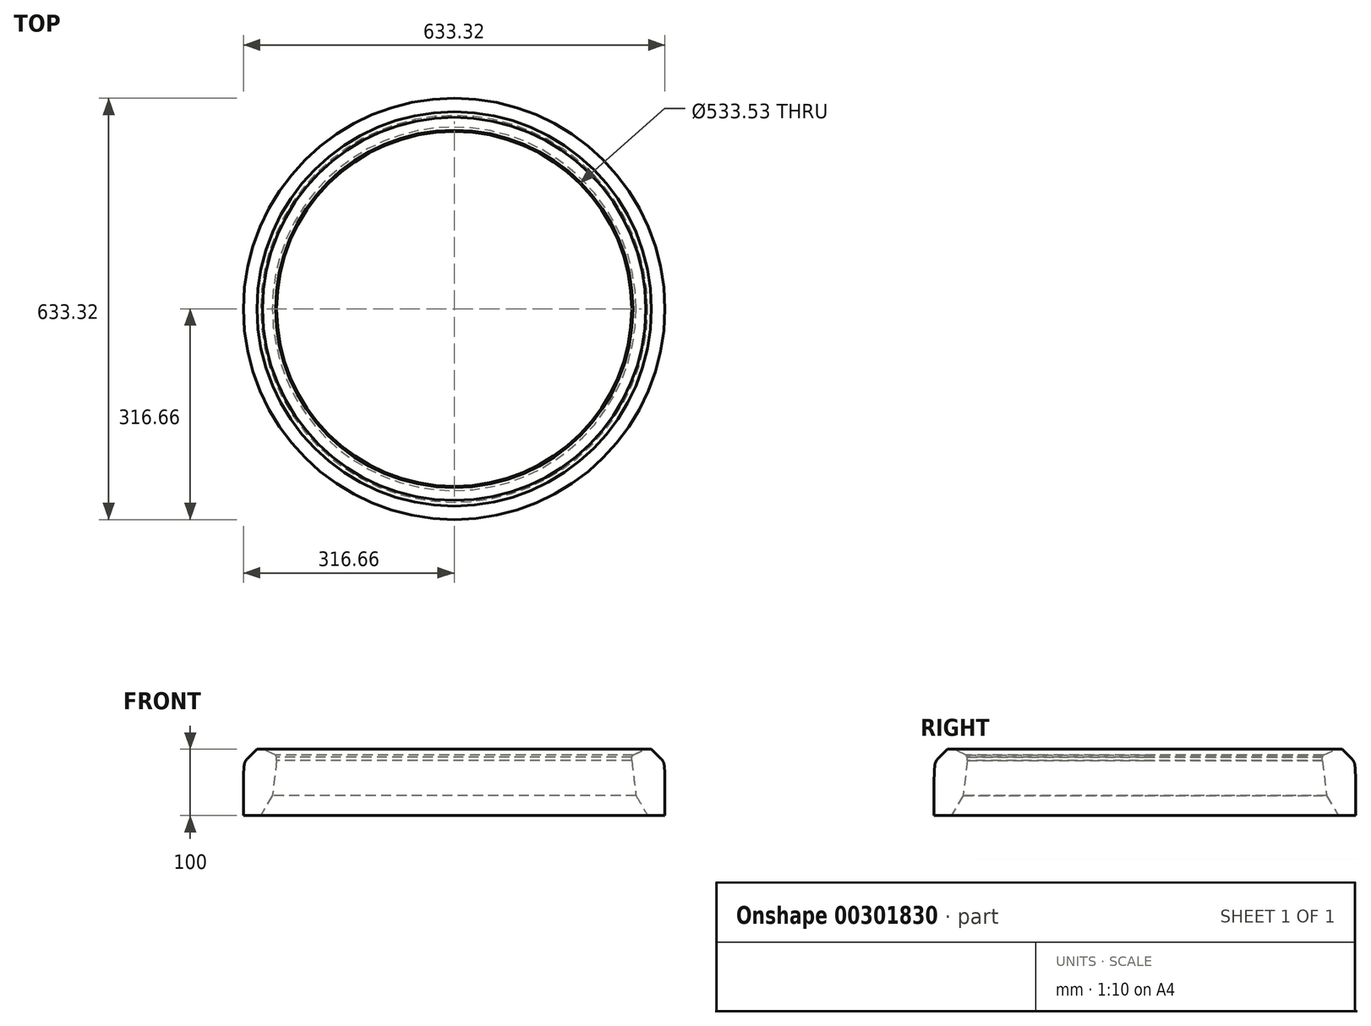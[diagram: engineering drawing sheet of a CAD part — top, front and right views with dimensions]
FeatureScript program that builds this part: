
annotation { "Feature Type Name" : "Feature", "Feature Type Description" : "" }
export const myFeature = defineFeature(function(context is Context, id is Id, definition is map)
    precondition{}
    {
        {
            var Q0;
            Q0=qCreatedBy(makeId("Front.planeOp"),FACE);
            var sketch = newSketch(context, id + "F0", { "sketchPlane" : qUnion([Q0])});
            skLineSegment(sketch, "E0", {"start": v(0, 0) * mm, "end": v(0, 100) * mm});
            skLineSegment(sketch, "E1", {"start": v(-316.65, 55) * mm, "end": v(-316.65, 0) * mm});
            skLineSegment(sketch, "E2", {"start": v(-290.69, 0) * mm, "end": v(-316.66, 0) * mm});
            skLineSegment(sketch, "E3", {"start": v(-296.34, 100) * mm, "end": v(-288, 100) * mm});
            skArc(sketch, "E4", {"start": v(-315.58, 75.7) * mm, "mid": v(-316.39, 65.36) * mm, "end": v(-316.65, 55) * mm});
            skArc(sketch, "E5", {"start": v(-310.98, 85.35) * mm, "mid": v(-314.11, 80.92) * mm, "end": v(-315.58, 75.7) * mm});
            skLineSegment(sketch, "E6", {"start": v(-296.34, 100) * mm, "end": v(-310.98, 85.35) * mm});
            skLineSegment(sketch, "E7", {"start": v(-288, 100) * mm, "end": v(-268.6, 90.95) * mm});
            skLineSegment(sketch, "E8", {"start": v(-266.76, 83) * mm, "end": v(-273.25, 30.2) * mm});
            skPoint(sketch, "E9.endSnap0", {"position": v(-268.21, 90.77) * mm});
            skLineSegment(sketch, "E10.trimOffspring", {"start": v(-268.6, 90.95) * mm, "end": v(-266.77, 87.77) * mm});
            skLineSegment(sketch, "E11.trimOffspring", {"start": v(-266.77, 87.77) * mm, "end": v(-266.76, 83) * mm});
            skPoint(sketch, "E9.end.orphan", {"position": v(-262.17, 90.77) * mm});
            skPoint(sketch, "E12.trimOffspring.end.orphan", {"position": v(-248.42, 81.54) * mm});
            skPoint(sketch, "E13.orphan", {"position": v(-270.75, 50.58) * mm});
            skLineSegment(sketch, "E14", {"start": v(-273.25, 30.2) * mm, "end": v(-290.69, 0) * mm});
            skPoint(sketch, "E15.orphan", {"position": v(-10.37, 0) * mm});
            skPoint(sketch, "E16.end.orphan", {"position": v(-273.25, 22.34) * mm});
            skPoint(sketch, "E17.start.orphan", {"position": v(-270.75, 30.2) * mm});
            skLineSegment(sketch, "E18", {"start": v(0, 150.82) * mm, "end": v(0, 120.73) * mm});
            skSolve(sketch);
        }
        {
            var Q0;
            Q0 = qSketchRegion(id + "F0", true);
            var Q1;
            Q1=sQuery(id+"F0.wireOp",EDGE,"E18");
            revolve(context, id + "F1", {"entities" : qUnion([Q0]), "axis" : qUnion([Q1]), "revolveType" : RevolveType.FULL});
        }
    });
